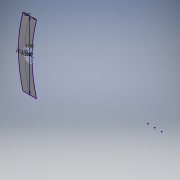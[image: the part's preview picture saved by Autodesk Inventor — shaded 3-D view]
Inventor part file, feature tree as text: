
AUTODESK INVENTOR PART (.ipt)
format: ipt  version: 2016 (Build 200138000, 138)  size: 164,352 bytes
history: native  units: mm
features: sketch x3, extrude x2, projected_geometry x2, hole x1, mirror x1
ambient origin geometry x8: Origin, YZ Plane, XZ Plane, XY Plane, X Axis, Y Axis, Z Axis, Center Point
bodies: Solid1 (feature_tree)
feature tree (9):
  sketch  "Sketch1"  dims[d0=1500.0mm d1=100.0mm]
  extrude  "Extrusion1"  Depth=1500.0mm
  extrude  "Extrusion2"  Depth=150.0mm
  hole  "Hole2"  [1 undecoded]
  mirror  "Mirror1"
  sketch  "Sketch2"  dims[d2=300.0mm d3=150.0mm]
  projected_geometry  "Projected Loop2"
  sketch  "Sketch3"  dims[d4=150.0mm d5=5.0mm d6=0.0mm d9=300.0mm d10=16.0mm d11=266.893054mm d12=60.0mm d14=53.378611mm d15=10.0mm d17=10.0mm d26=16.0mm d27=16.0mm d28=60.0mm d30=53.378611mm d31=10.0mm d33=10.0mm d35=6.2mm d36=6.0mm d37=4.0mm d38=2.0mm d39=90.0deg d40=8.0mm d41=20.594885mm d42=72.0mm d43=60.0mm d45=360.0deg d54=1.75mm d55=0.0mm]
  projected_geometry  "Projected Loop3"
note: 1 required parameter value undecoded (feature->parameter linkage not recoverable at this tier; creation-order binding heuristic only, values carry confidence <= 0.55)
